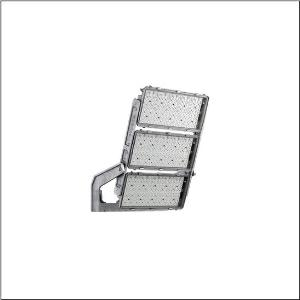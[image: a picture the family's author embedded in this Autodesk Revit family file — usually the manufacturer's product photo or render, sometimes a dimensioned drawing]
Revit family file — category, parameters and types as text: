
# Revit family: floodlight_fl_11_maxi_pro_remote___pl64_5xa779427v01aa_f124
name_source: partatom
category: Lighting Fixtures
units: mm (PartAtom-declared; Revit-internal decimal feet)

## family parameters
Cut with Voids When Loaded = No
Host = Face
Light Source = No
Part Type = Normal
Room Calculation Point = No
Round Connector Dimension = Use Diameter
Shared = No

## types (1)
- --- (1 x LED, 220410 lm, 1540.1 W, 5000K)
    Apparent Load = 1540 VA
    CIE Flux Codes = 28 79 98 100 100
    Color Rendering = 70
    Color Temperature = 5000K
    Default Elevation = 1800 mm
    Description = Floodlight FL 11  maxi  pro Remote floodlight; light control with lens of PMMA; cover panel of toughened safety glass, transparent; light distribution: PL64, asymmetric direct distribution, LEDcolour temperature: 5000K, rated luminous flux: 220.410lm, colour rendering: CRI > 70, light colour: 750; luminous efficacy: 143lm/W; brightness control: DALI 2 (1 DALI address); with terminal, 8-pole, max. 2.5mm², mains connection: 220..240V/380..400V AC, 50/60Hz, surge voltage resistance: line to ground: 10kV, ECG replaceable separately, no afterglow with DALI off / DMX off command, LED unit replaceable without ESD environment, dustproof LED module, dimming range 10..100%; 1540W floodlight with 2x LED unit of diecast aluminium, coated grey; length: 713mm / width: 651mm / height: 338mm; mounting bracket, of diecast aluminium, uncoated, natural, equipment: Power, protection rating (complete): IP66; insulation class (complete): insulation class I (protective earthing); certification: CE, ENEC, VDE; ball protection: ball impact resistance with accessories, impact resistance: IK07; only for outdoor installations, rated ambient temperature 10°C, permissible operating ambient temperature: -40..+30°C, permissible storage temperature: -40..+85°C; packaging unit: 1 piece

Light Distribution: PL64
    Height = 320 mm
    Lamp = 1 x LED
    Lamp Light Flux = 220410 lm
    Lamp Power = 1540.1 W
    Lamp count = 1
    Length = 1002 mm
    Luminous efficacy = 143 lm/W
    Manufacturer = Siteco
    ModVariant = No
    Model = 5XA779427V01AA
    Mounting Place = Ceiling
    Mounting Type = Surface mounted
    Number of Poles = 1
    OnlyDefault = Yes
    Power Factor = 1
    Product Name = Floodlight FL 11 maxi pro Remote | PL64
    Product group = floodlight | ceiling mounted
    ProductGroupID = 303
    Protection Class = Protection class I
    Protection Degree = IP 66
    RLX_Detail_Level = 1
    RLX_Emergency_Light_Flux = 0 lm
    RLX_Emergency_Type = 0
    RLX_Emergency_Type_DB = No
    RlxData = <blob elided: 52421 chars, md5=5d02041a>
    Socket = socket
    Standby Power = 0 W
    System Light Flux = 220410 lm
    System Power = 1540 W
    Type Comments = factory setting: luminous flux: 100 % | dim-lin: 254 | 1080 mA
    Type Image = l_1006784.jpg
    URL = http://relux.com
    VarID = @adj_057557
    Voltage = 0 V
    Weight = 0.00 kg
    Width = 655 mm

## geometry (parser evidence)
native form markers: Blend x4, Sweep x14
no freeform markers — native parametric forms only
